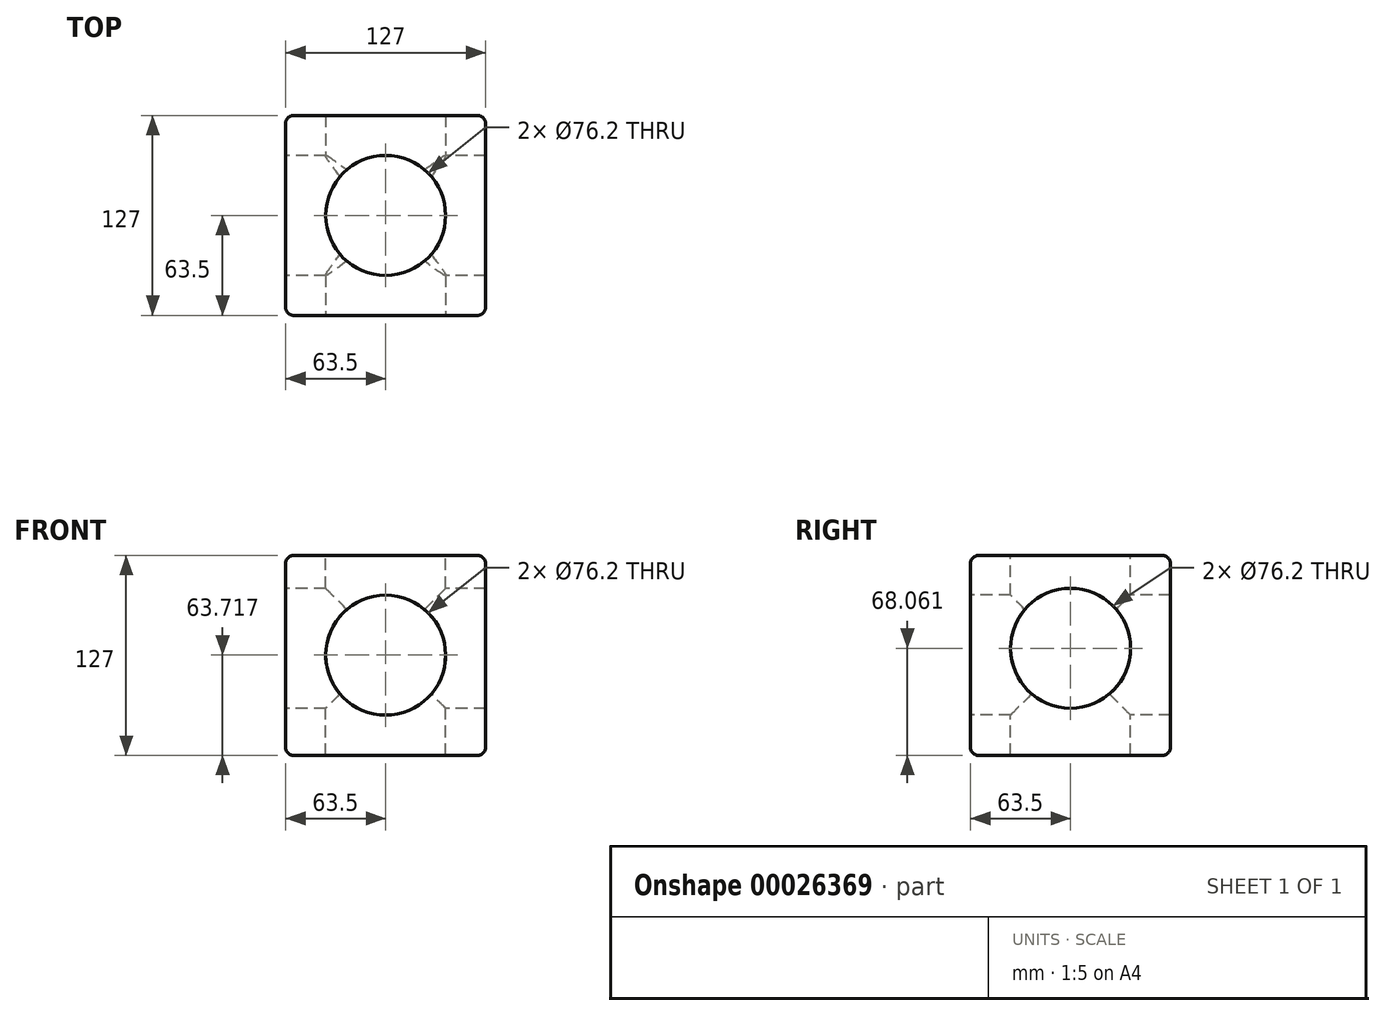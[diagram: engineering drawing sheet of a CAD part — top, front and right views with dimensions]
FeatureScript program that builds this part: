
annotation { "Feature Type Name" : "Feature", "Feature Type Description" : "" }
export const myFeature = defineFeature(function(context is Context, id is Id, definition is map)
    precondition{}
    {
        {
            var Q0;
            Q0=qCreatedBy(makeId("Top.planeOp"),FACE);
            var sketch = newSketch(context, id + "F0", { "sketchPlane" : qUnion([Q0])});
            skLineSegment(sketch, "E0.rect.bottom", {"start": v(-63.5, 63.5) * mm, "end": v(63.5, 63.5) * mm});
            skLineSegment(sketch, "E0.rect.top", {"start": v(-63.5, -63.5) * mm, "end": v(63.5, -63.5) * mm});
            skLineSegment(sketch, "E0.rect.left", {"start": v(-63.5, 63.5) * mm, "end": v(-63.5, -63.5) * mm});
            skLineSegment(sketch, "E0.rect.right", {"start": v(63.5, 63.5) * mm, "end": v(63.5, -63.5) * mm});
            skPoint(sketch, "E0.rect.middle", {"position": v(0, 0) * mm});
            skSolve(sketch);
        }
        {
            var Q0;
            Q0=makeQuery(id+"F0.imprint","IMPRINT",FACE,{"disambiguationData":[TD([[makeQuery(id+"F0.imprint","IMPRINT",EDGE,{"derivedFrom":sQuery(id+"F0.wireOp",EDGE,"E0.rect.bottom")}),-1.0]])]});
            extrude(context, id + "F1", {"entities" : qUnion([Q0]), "depth" : 127 * mm});
        }
        {
            var Q0;
            Q0=makeQuery(id+"F1.opExtrude","CAP_FACE",FACE,{"disambiguationData":[OSD([sQuery(id+"F0.wireOp",EDGE,"E0.rect.bottom"),sQuery(id+"F0.wireOp",EDGE,"E0.rect.top"),sQuery(id+"F0.wireOp",EDGE,"E0.rect.left"),sQuery(id+"F0.wireOp",EDGE,"E0.rect.right")])],"isStart":false});
            var sketch = newSketch(context, id + "F2", { "sketchPlane" : qUnion([Q0])});
            skCircle(sketch, "E1", {"center": v(0, 0) * mm, "radius": 38.1 * mm});
            skSolve(sketch);
        }
        {
            var Q0;
            Q0=makeQuery(id+"F2.imprint","IMPRINT",FACE,{"disambiguationData":[TD([[makeQuery(id+"F2.imprint","IMPRINT",EDGE,{"derivedFrom":sQuery(id+"F2.wireOp",EDGE,"E1")}),1.0]])]});
            extrude(context, id + "F3", {"entities" : qUnion([Q0]), "operationType" : NewBodyOperationType.REMOVE, "oppositeDirection" : true, "depth" : 127 * mm});
        }
        {
            var Q0;
            Q0=makeQuery(id+"F1.opExtrude","SWEPT_FACE",FACE,{"disambiguationData":[OSD([sQuery(id+"F0.wireOp",EDGE,"E0.rect.left")])]});
            var sketch = newSketch(context, id + "F4", { "sketchPlane" : qUnion([Q0])});
            skCircle(sketch, "E2", {"center": v(0, 68.06) * mm, "radius": 38.1 * mm});
            skSolve(sketch);
        }
        {
            var Q0;
            Q0=makeQuery(id+"F4.imprint","IMPRINT",FACE,{"disambiguationData":[TD([[makeQuery(id+"F4.imprint","IMPRINT",EDGE,{"derivedFrom":sQuery(id+"F4.wireOp",EDGE,"E2")}),1.0]])]});
            extrude(context, id + "F5", {"entities" : qUnion([Q0]), "operationType" : NewBodyOperationType.REMOVE, "oppositeDirection" : true, "depth" : 127 * mm});
        }
        {
            var Q0;
            Q0=makeQuery(id+"F1.opExtrude","SWEPT_FACE",FACE,{"disambiguationData":[OSD([sQuery(id+"F0.wireOp",EDGE,"E0.rect.top")])]});
            var sketch = newSketch(context, id + "F6", { "sketchPlane" : qUnion([Q0])});
            skCircle(sketch, "E3", {"center": v(0, 63.72) * mm, "radius": 38.1 * mm});
            skSolve(sketch);
        }
        {
            var Q0;
            Q0=makeQuery(id+"F6.imprint","IMPRINT",FACE,{"disambiguationData":[TD([[makeQuery(id+"F6.imprint","IMPRINT",EDGE,{"derivedFrom":sQuery(id+"F6.wireOp",EDGE,"E3")}),1.0]])]});
            extrude(context, id + "F7", {"entities" : qUnion([Q0]), "operationType" : NewBodyOperationType.REMOVE, "oppositeDirection" : true, "depth" : 127 * mm});
        }
        {
            var Q0;
            Q0=makeQuery(id+"F1.opExtrude","CAP_EDGE",EDGE,{"disambiguationData":[OSD([sQuery(id+"F0.wireOp",EDGE,"E0.rect.top")])],"isStart":false});
            var Q1;
            Q1=makeQuery(id+"F1.opExtrude","CAP_EDGE",EDGE,{"disambiguationData":[OSD([sQuery(id+"F0.wireOp",EDGE,"E0.rect.right")])],"isStart":false});
            var Q2;
            Q2=makeQuery(id+"F3.boolean.opBoolean","COPY",EDGE,{"derivedFrom":makeQuery(id+"F3.opExtrude","CAP_EDGE",EDGE,{"disambiguationData":[OSD([sQuery(id+"F2.wireOp",EDGE,"E1")])],"isStart":true})});
            var Q3;
            Q3=makeQuery(id+"F5.boolean.opBoolean","COPY",EDGE,{"derivedFrom":makeQuery(id+"F5.opExtrude","CAP_EDGE",EDGE,{"disambiguationData":[OSD([sQuery(id+"F4.wireOp",EDGE,"E2")])],"isStart":false})});
            var Q4;
            Q4=makeQuery(id+"F7.boolean.opBoolean","COPY",EDGE,{"derivedFrom":makeQuery(id+"F7.opExtrude","CAP_EDGE",EDGE,{"disambiguationData":[OSD([sQuery(id+"F6.wireOp",EDGE,"E3")])],"isStart":true})});
            var Q5;
            Q5=makeQuery(id+"F3.boolean.opBoolean","COPY",EDGE,{"derivedFrom":makeQuery(id+"F3.opExtrude","CAP_EDGE",EDGE,{"disambiguationData":[OSD([sQuery(id+"F2.wireOp",EDGE,"E1")])],"isStart":false})});
            var Q6;
            Q6=makeQuery(id+"F5.boolean.opBoolean","COPY",EDGE,{"derivedFrom":makeQuery(id+"F5.opExtrude","CAP_EDGE",EDGE,{"disambiguationData":[OSD([sQuery(id+"F4.wireOp",EDGE,"E2")])],"isStart":true})});
            var Q7;
            Q7=makeQuery(id+"F7.boolean.opBoolean","COPY",EDGE,{"derivedFrom":makeQuery(id+"F7.opExtrude","CAP_EDGE",EDGE,{"disambiguationData":[OSD([sQuery(id+"F6.wireOp",EDGE,"E3")])],"isStart":false})});
            var Q8;
            Q8=makeQuery(id+"F1.opExtrude","CAP_EDGE",EDGE,{"disambiguationData":[OSD([sQuery(id+"F0.wireOp",EDGE,"E0.rect.bottom")])],"isStart":false});
            var Q9;
            Q9=makeQuery(id+"F1.opExtrude","CAP_EDGE",EDGE,{"disambiguationData":[OSD([sQuery(id+"F0.wireOp",EDGE,"E0.rect.left")])],"isStart":false});
            var Q10;
            Q10=makeQuery(id+"F1.opExtrude","SWEPT_EDGE",EDGE,{"disambiguationData":[OSD([sQuery(id+"F0.wireOp",EDGE,"E0.rect.top"),sQuery(id+"F0.wireOp",EDGE,"E0.rect.left")])]});
            var Q11;
            Q11=makeQuery(id+"F1.opExtrude","CAP_EDGE",EDGE,{"disambiguationData":[OSD([sQuery(id+"F0.wireOp",EDGE,"E0.rect.top")])],"isStart":true});
            var Q12;
            Q12=makeQuery(id+"F1.opExtrude","CAP_EDGE",EDGE,{"disambiguationData":[OSD([sQuery(id+"F0.wireOp",EDGE,"E0.rect.right")])],"isStart":true});
            var Q13;
            Q13=makeQuery(id+"F1.opExtrude","SWEPT_EDGE",EDGE,{"disambiguationData":[OSD([sQuery(id+"F0.wireOp",EDGE,"E0.rect.bottom"),sQuery(id+"F0.wireOp",EDGE,"E0.rect.right")])]});
            var Q14;
            Q14=makeQuery(id+"F1.opExtrude","SWEPT_EDGE",EDGE,{"disambiguationData":[OSD([sQuery(id+"F0.wireOp",EDGE,"E0.rect.top"),sQuery(id+"F0.wireOp",EDGE,"E0.rect.right")])]});
            fillet(context, id + "F8", {"entities" : qUnion([Q0, Q1, Q2, Q3, Q4, Q5, Q6, Q7, Q8, Q9, Q10, Q11, Q12, Q13, Q14]), "radius" : 5.08 * mm, "tangentPropagation" : true, "allowEdgeOverflow" : false});
        }
        {
            var Q0;
            Q0=makeQuery(id+"F1.opExtrude","CAP_EDGE",EDGE,{"disambiguationData":[OSD([sQuery(id+"F0.wireOp",EDGE,"E0.rect.bottom")])],"isStart":true});
            var Q1;
            Q1=makeQuery(id+"F1.opExtrude","SWEPT_EDGE",EDGE,{"disambiguationData":[OSD([sQuery(id+"F0.wireOp",EDGE,"E0.rect.bottom"),sQuery(id+"F0.wireOp",EDGE,"E0.rect.left")])]});
            var Q2;
            Q2=makeQuery(id+"F1.opExtrude","CAP_EDGE",EDGE,{"disambiguationData":[OSD([sQuery(id+"F0.wireOp",EDGE,"E0.rect.left")])],"isStart":true});
            var Q3;
            {var subQ0=sQuery(id+"F0.wireOp",EDGE,"E0.rect.top");Q3=makeQuery(id+"F8.opFillet","BLEND_EDGE",EDGE,{"blendedFrom":[makeQuery(id+"F1.opExtrude","CAP_EDGE",EDGE,{"disambiguationData":[OSD([subQ0])],"isStart":true}),makeQuery(id+"F1.opExtrude","CAP_FACE",FACE,{"disambiguationData":[OSD([sQuery(id+"F0.wireOp",EDGE,"E0.rect.bottom"),subQ0,sQuery(id+"F0.wireOp",EDGE,"E0.rect.left"),sQuery(id+"F0.wireOp",EDGE,"E0.rect.right")])],"isStart":true})],"blendedInto":[makeQuery(id+"F1.opExtrude","CAP_FACE",FACE,{"disambiguationData":[OSD([sQuery(id+"F0.wireOp",EDGE,"E0.rect.bottom"),subQ0,sQuery(id+"F0.wireOp",EDGE,"E0.rect.left"),sQuery(id+"F0.wireOp",EDGE,"E0.rect.right")])],"isStart":true})]});}
            fillet(context, id + "F9", {"entities" : qUnion([Q0, Q1, Q2, Q3]), "radius" : 5.08 * mm, "tangentPropagation" : true, "allowEdgeOverflow" : false});
        }
    });
